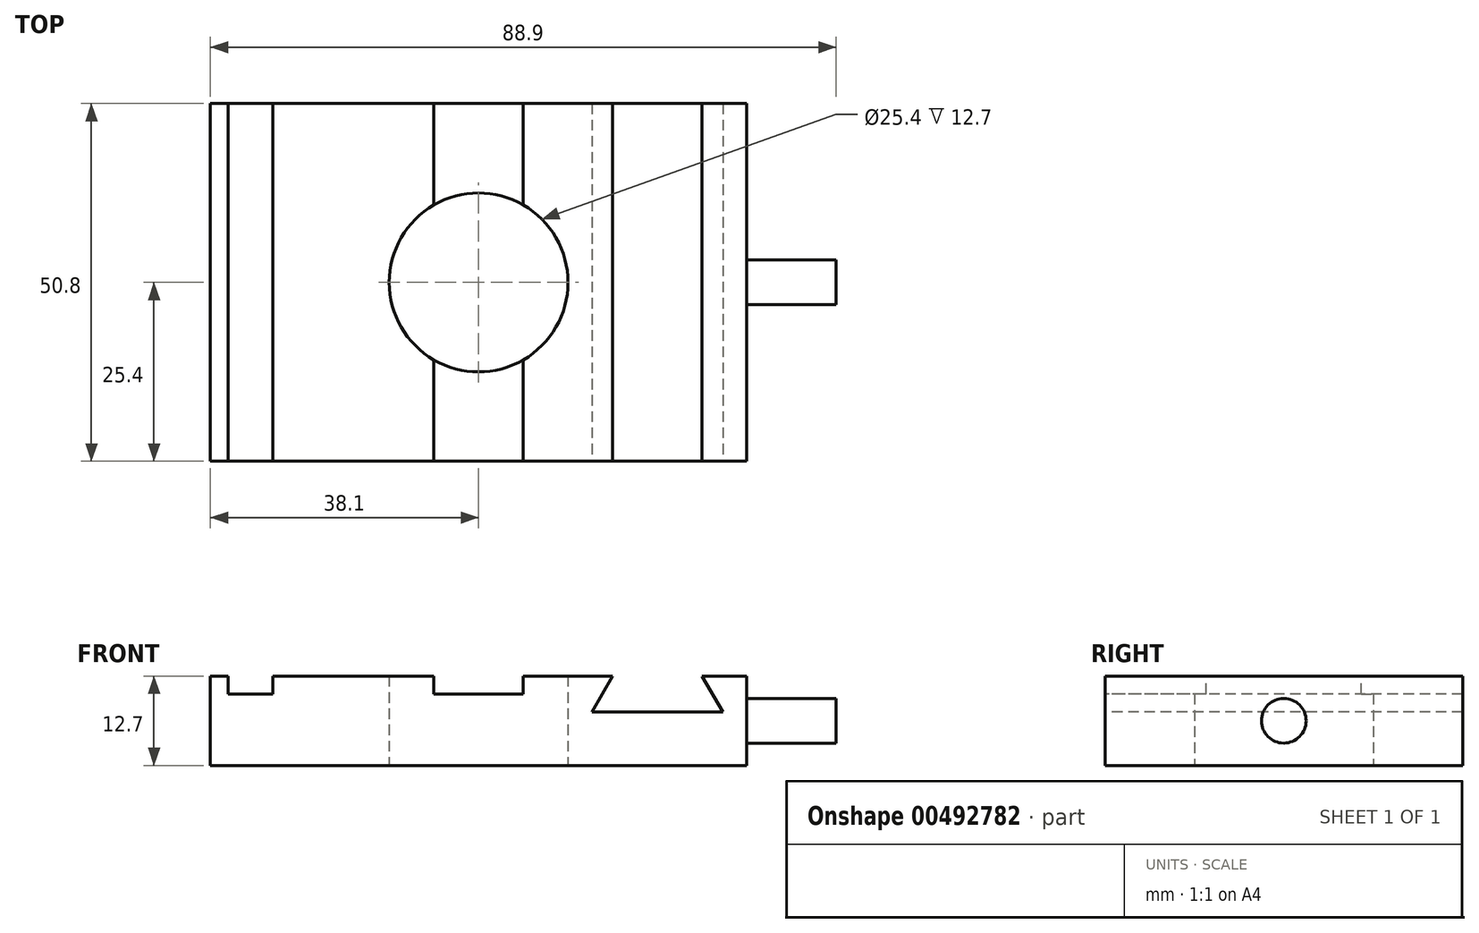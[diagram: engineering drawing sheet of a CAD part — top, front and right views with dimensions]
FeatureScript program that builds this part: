
annotation { "Feature Type Name" : "Feature", "Feature Type Description" : "" }
export const myFeature = defineFeature(function(context is Context, id is Id, definition is map)
    precondition{}
    {
        {
            var Q0;
            Q0=qCreatedBy(makeId("Top.planeOp"),FACE);
            var sketch = newSketch(context, id + "F0", { "sketchPlane" : qUnion([Q0])});
            skLineSegment(sketch, "E0", {"start": v(-38.1, 25.4) * mm, "end": v(38.1, 25.4) * mm});
            skLineSegment(sketch, "E1", {"start": v(38.1, 25.4) * mm, "end": v(38.1, -25.4) * mm});
            skLineSegment(sketch, "E2", {"start": v(38.1, -25.4) * mm, "end": v(-38.1, -25.4) * mm});
            skLineSegment(sketch, "E3", {"start": v(-38.1, 25.4) * mm, "end": v(-38.1, -25.4) * mm});
            skCircle(sketch, "E4", {"center": v(0, 0) * mm, "radius": 12.7 * mm});
            skSolve(sketch);
        }
        {
            var Q0;
            Q0=makeQuery(id+"F0.imprint","IMPRINT",FACE,{"disambiguationData":[TD([[makeQuery(id+"F0.imprint","IMPRINT",EDGE,{"derivedFrom":sQuery(id+"F0.wireOp",EDGE,"E0")}),-1.0]])]});
            extrude(context, id + "F1", {"entities" : qUnion([Q0]), "depth" : 12.7 * mm, "offsetDistance" : 25.4 * mm});
        }
        {
            var Q0;
            Q0=makeQuery(id+"F1.opExtrude","CAP_FACE",FACE,{"disambiguationData":[OSD([sQuery(id+"F0.wireOp",EDGE,"E0"),sQuery(id+"F0.wireOp",EDGE,"E1"),sQuery(id+"F0.wireOp",EDGE,"E2"),sQuery(id+"F0.wireOp",EDGE,"E3"),sQuery(id+"F0.wireOp",EDGE,"E4")])],"isStart":false});
            var sketch = newSketch(context, id + "F2", { "sketchPlane" : qUnion([Q0])});
            skLineSegment(sketch, "E5", {"start": v(-35.56, 25.4) * mm, "end": v(-35.56, -25.4) * mm});
            skLineSegment(sketch, "E6", {"start": v(-29.21, 25.4) * mm, "end": v(-29.21, -25.4) * mm});
            skLineSegment(sketch, "E7", {"start": v(-6.35, 25.4) * mm, "end": v(-6.35, -25.4) * mm});
            skLineSegment(sketch, "E8", {"start": v(6.35, 25.4) * mm, "end": v(6.35, -25.4) * mm});
            skLineSegment(sketch, "E9", {"start": v(0, 25.4) * mm, "end": v(0, -25.4) * mm, "construction": true});
            skSolve(sketch);
        }
        {
            var Q0;
            {var subQ0=sQuery(id+"F2.wireOp",EDGE,"E5");Q0=makeQuery(id+"F2.imprint","IMPRINT",FACE,{"disambiguationData":[TD([[makeQuery(id+"F2.imprint","IMPRINT",EDGE,{"derivedFrom":subQ0}),1.0]])]});}
            var Q1;
            {var subQ0=sQuery(id+"F2.wireOp",EDGE,"E7");var subQ1=makeQuery(id+"F1.opExtrude","CAP_EDGE",EDGE,{"disambiguationData":[OSD([sQuery(id+"F0.wireOp",EDGE,"E0")])],"isStart":false});var subQ2=makeQuery(id+"F2.imprint","INTERSECT",VERTEX,{"derivedFrom":[subQ1,subQ0]});Q1=makeQuery(id+"F2.imprint","IMPRINT",FACE,{"disambiguationData":[TD([[makeQuery(id+"F2.imprint","IMPRINT",EDGE,{"disambiguationData":[TD([[subQ2,-1.0]])],"derivedFrom":subQ0}),1.0]])]});}
            var Q2;
            {var subQ0=sQuery(id+"F2.wireOp",EDGE,"E7");var subQ1=makeQuery(id+"F1.opExtrude","CAP_EDGE",EDGE,{"disambiguationData":[OSD([sQuery(id+"F0.wireOp",EDGE,"E2")])],"isStart":false});var subQ2=makeQuery(id+"F2.imprint","INTERSECT",VERTEX,{"derivedFrom":[subQ1,subQ0]});Q2=makeQuery(id+"F2.imprint","IMPRINT",FACE,{"disambiguationData":[TD([[makeQuery(id+"F2.imprint","IMPRINT",EDGE,{"disambiguationData":[TD([[subQ2,1.0]])],"derivedFrom":subQ0}),1.0]])]});}
            extrude(context, id + "F3", {"entities" : qUnion([Q0, Q1, Q2]), "operationType" : NewBodyOperationType.REMOVE, "oppositeDirection" : true, "depth" : 2.54 * mm, "offsetDistance" : 25.4 * mm});
        }
        {
            var Q0;
            Q0=makeQuery(id+"F1.opExtrude","SWEPT_FACE",FACE,{"disambiguationData":[OSD([sQuery(id+"F0.wireOp",EDGE,"E2")])]});
            var sketch = newSketch(context, id + "F4", { "sketchPlane" : qUnion([Q0])});
            skLineSegment(sketch, "E10", {"start": v(19.05, 12.7) * mm, "end": v(16.12, 7.62) * mm});
            skLineSegment(sketch, "E11", {"start": v(16.12, 7.62) * mm, "end": v(34.68, 7.62) * mm});
            skLineSegment(sketch, "E12", {"start": v(34.68, 7.62) * mm, "end": v(31.75, 12.7) * mm});
            skLineSegment(sketch, "E13", {"start": v(31.75, 12.7) * mm, "end": v(19.05, 12.7) * mm});
            skLineSegment(sketch, "E14", {"start": v(25.4, 7.62) * mm, "end": v(25.4, 12.7) * mm, "construction": true});
            skSolve(sketch);
        }
        {
            var Q0;
            Q0=makeQuery(id+"F4.imprint","IMPRINT",FACE,{"disambiguationData":[TD([[makeQuery(id+"F4.imprint","IMPRINT",EDGE,{"derivedFrom":sQuery(id+"F4.wireOp",EDGE,"E10")}),1.0]])]});
            extrude(context, id + "F5", {"entities" : qUnion([Q0]), "operationType" : NewBodyOperationType.REMOVE, "endBound" : BoundingType.UP_TO_NEXT, "oppositeDirection" : true, "depth" : 50.8 * mm, "offsetDistance" : 25.4 * mm});
        }
        {
            var Q0;
            Q0=makeQuery(id+"F1.opExtrude","SWEPT_FACE",FACE,{"disambiguationData":[OSD([sQuery(id+"F0.wireOp",EDGE,"E1")])]});
            var sketch = newSketch(context, id + "F6", { "sketchPlane" : qUnion([Q0])});
            skCircle(sketch, "E15", {"center": v(0, 6.35) * mm, "radius": 3.18 * mm});
            skPoint(sketch, "E15.centerSnap0", {"position": v(25.4, 6.35) * mm});
            skPoint(sketch, "E15.centerSnap1", {"position": v(0, 12.7) * mm});
            skSolve(sketch);
        }
        {
            var Q0;
            Q0=makeQuery(id+"F6.imprint","IMPRINT",FACE,{"disambiguationData":[TD([[makeQuery(id+"F6.imprint","IMPRINT",EDGE,{"derivedFrom":sQuery(id+"F6.wireOp",EDGE,"E15")}),1.0]])]});
            extrude(context, id + "F7", {"entities" : qUnion([Q0]), "operationType" : NewBodyOperationType.ADD, "depth" : 12.7 * mm, "offsetDistance" : 25.4 * mm});
        }
    });
